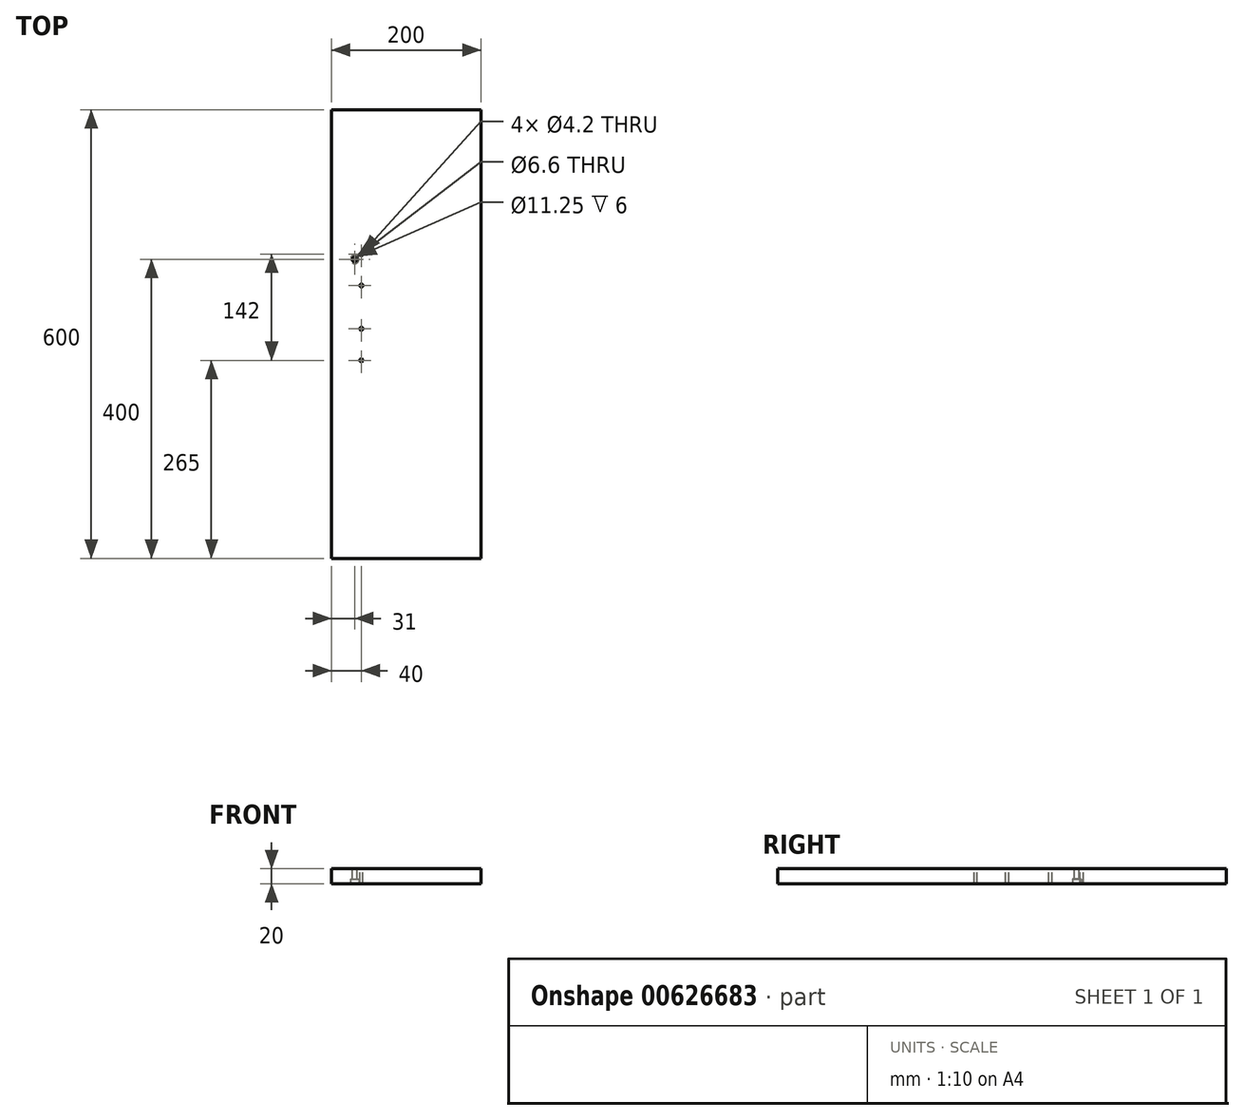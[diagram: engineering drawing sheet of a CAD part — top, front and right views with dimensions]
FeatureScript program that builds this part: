
annotation { "Feature Type Name" : "Feature", "Feature Type Description" : "" }
export const myFeature = defineFeature(function(context is Context, id is Id, definition is map)
    precondition{}
    {
        {
            var Q0;
            Q0=qCreatedBy(makeId("Top.planeOp"),FACE);
            var sketch = newSketch(context, id + "F0", { "sketchPlane" : qUnion([Q0])});
            skLineSegment(sketch, "E0.bottom", {"start": v(-100, 300) * mm, "end": v(100, 300) * mm});
            skLineSegment(sketch, "E0.top", {"start": v(-100, -300) * mm, "end": v(100, -300) * mm});
            skLineSegment(sketch, "E0.left", {"start": v(-100, 300) * mm, "end": v(-100, -300) * mm});
            skLineSegment(sketch, "E0.right", {"start": v(100, 300) * mm, "end": v(100, -300) * mm});
            skPoint(sketch, "E0.middle", {"position": v(0, 0) * mm});
            skSolve(sketch);
        }
        {
            var Q0;
            Q0=makeQuery(id+"F0.imprint","IMPRINT",FACE,{"disambiguationData":[TD([[makeQuery(id+"F0.imprint","IMPRINT",EDGE,{"derivedFrom":sQuery(id+"F0.wireOp",EDGE,"E0.bottom")}),-1.0]])]});
            extrude(context, id + "F1", {"entities" : qUnion([Q0]), "depth" : 20 * mm, "offsetDistance" : 25 * mm});
        }
        {
            var Q0;
            Q0=makeQuery(id+"F1.opExtrude","CAP_FACE",FACE,{"disambiguationData":[OSD([sQuery(id+"F0.wireOp",EDGE,"E0.bottom"),sQuery(id+"F0.wireOp",EDGE,"E0.top"),sQuery(id+"F0.wireOp",EDGE,"E0.left"),sQuery(id+"F0.wireOp",EDGE,"E0.right")])],"isStart":false});
            var sketch = newSketch(context, id + "F2", { "sketchPlane" : qUnion([Q0])});
            skPoint(sketch, "E1", {"position": v(-69, 100) * mm});
            skPoint(sketch, "E2", {"position": v(-60, 107) * mm});
            skPoint(sketch, "E3", {"position": v(-60, 65) * mm});
            skPoint(sketch, "E4", {"position": v(-60, 7) * mm});
            skPoint(sketch, "E5", {"position": v(-60, -35) * mm});
            skSolve(sketch);
        }
        {
            var Q0;
            Q0=sQuery(id+"F2.wireOp",VERTEX,"E2");
            var Q1;
            Q1=sQuery(id+"F2.wireOp",VERTEX,"E3");
            var Q2;
            Q2=sQuery(id+"F2.wireOp",VERTEX,"E4");
            var Q3;
            Q3=sQuery(id+"F2.wireOp",VERTEX,"E5");
            var Q4;
            Q4=makeQuery(id+"F1.opExtrude","SWEPT_BODY",BODY,{"disambiguationData":[OSD([sQuery(id+"F0.wireOp",EDGE,"E0.bottom"),sQuery(id+"F0.wireOp",EDGE,"E0.top"),sQuery(id+"F0.wireOp",EDGE,"E0.left"),sQuery(id+"F0.wireOp",EDGE,"E0.right")])]});
            hole(context, id + "F3", {"style" : HoleStyle.SIMPLE, "endStyle" : HoleEndStyle.THROUGH, "standardTappedOrClearance" : lookupTablePath({ "standard" : "ISO", "engagement" : "75%", "pitch" : "0.8 mm", "size" : "M5", "type" : "Tapped" }), "standardBlindInLast" : lookupTablePath({ "standard" : "ISO", "engagement" : "75%", "pitch" : "0.8 mm", "size" : "M5", "type" : "Tapped" }), "holeDiameter" : 4.2 * mm, "majorDiameter" : 5 * mm, "showTappedDepth" : true, "isTappedThrough" : true, "tappedDepth" : 19.6 * mm, "tapClearance" : 3, "startFromSketch" : true, "locations" : qUnion([Q0, Q1, Q2, Q3]), "scope" : qUnion([Q4])});
        }
        {
            var Q0;
            Q0=sQuery(id+"F2.wireOp",VERTEX,"E1");
            var Q1;
            Q1=makeQuery(id+"F1.opExtrude","SWEPT_BODY",BODY,{"disambiguationData":[OSD([sQuery(id+"F0.wireOp",EDGE,"E0.bottom"),sQuery(id+"F0.wireOp",EDGE,"E0.top"),sQuery(id+"F0.wireOp",EDGE,"E0.left"),sQuery(id+"F0.wireOp",EDGE,"E0.right")])]});
            hole(context, id + "F4", {"style" : HoleStyle.SIMPLE, "endStyle" : HoleEndStyle.THROUGH, "standardTappedOrClearance" : lookupTablePath({ "standard" : "ISO", "fit" : "Normal", "size" : "M6", "type" : "Clearance" }), "standardBlindInLast" : lookupTablePath({ "fit" : "Standard", "standard" : "ISO", "size" : "M6", "type" : "Clearance" }), "holeDiameter" : 6.6 * mm, "majorDiameter" : 5 * mm, "isTappedThrough" : true, "tappedDepth" : 19.6 * mm, "tapClearance" : 3, "startFromSketch" : true, "locations" : qUnion([Q0]), "scope" : qUnion([Q1])});
        }
        {
            var Q0;
            Q0=makeQuery(id+"F1.opExtrude","CAP_FACE",FACE,{"disambiguationData":[OSD([sQuery(id+"F0.wireOp",EDGE,"E0.bottom"),sQuery(id+"F0.wireOp",EDGE,"E0.top"),sQuery(id+"F0.wireOp",EDGE,"E0.left"),sQuery(id+"F0.wireOp",EDGE,"E0.right")])],"isStart":true});
            var sketch = newSketch(context, id + "F5", { "sketchPlane" : qUnion([Q0])});
            skPoint(sketch, "E6", {"position": v(-69, -100) * mm});
            skSolve(sketch);
        }
        {
            var Q0;
            Q0=sQuery(id+"F5.wireOp",VERTEX,"E6");
            var Q1;
            Q1=makeQuery(id+"F1.opExtrude","SWEPT_BODY",BODY,{"disambiguationData":[OSD([sQuery(id+"F0.wireOp",EDGE,"E0.bottom"),sQuery(id+"F0.wireOp",EDGE,"E0.top"),sQuery(id+"F0.wireOp",EDGE,"E0.left"),sQuery(id+"F0.wireOp",EDGE,"E0.right")])]});
            hole(context, id + "F6", {"style" : HoleStyle.C_BORE, "endStyle" : HoleEndStyle.THROUGH, "standardTappedOrClearance" : lookupTablePath({ "standard" : "ISO", "fit" : "Normal", "size" : "M6", "type" : "Clearance" }), "standardBlindInLast" : lookupTablePath({ "fit" : "Standard", "standard" : "ISO", "size" : "M6", "type" : "Clearance" }), "holeDiameter" : 6.6 * mm, "cBoreDiameter" : 11.25 * mm, "cBoreDepth" : 6 * mm, "majorDiameter" : 5 * mm, "isTappedThrough" : true, "tappedDepth" : 19.6 * mm, "tapClearance" : 3, "startFromSketch" : true, "locations" : qUnion([Q0]), "scope" : qUnion([Q1])});
        }
    });
